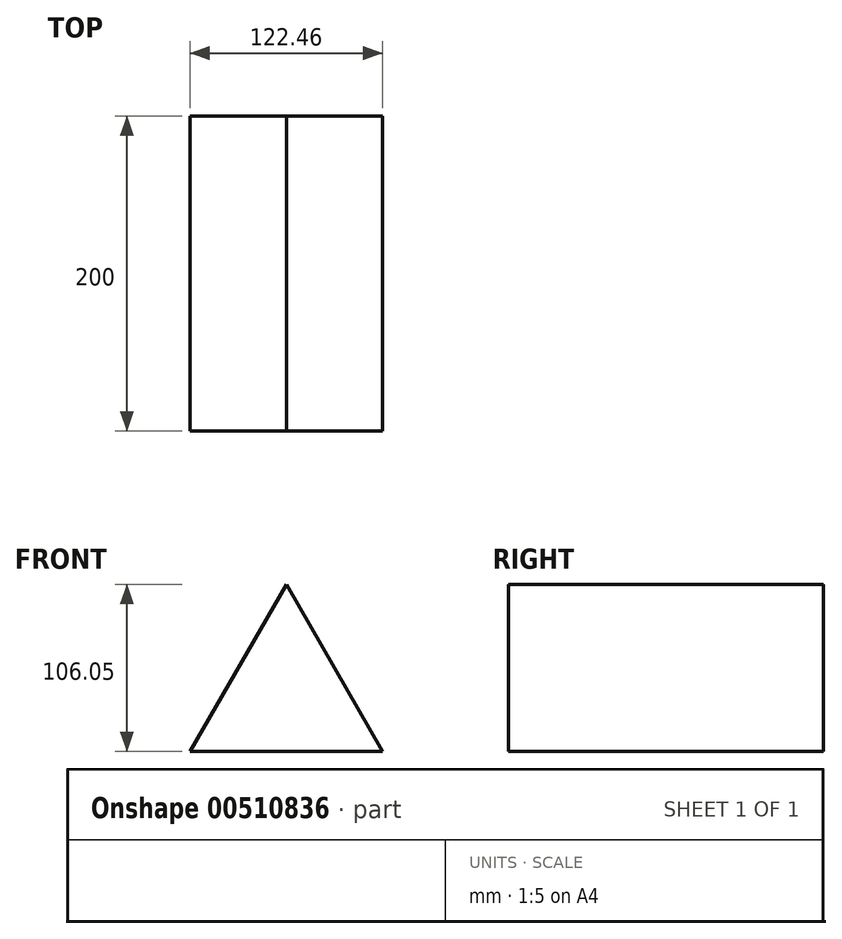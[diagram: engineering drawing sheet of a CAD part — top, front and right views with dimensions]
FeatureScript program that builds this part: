
annotation { "Feature Type Name" : "Feature", "Feature Type Description" : "" }
export const myFeature = defineFeature(function(context is Context, id is Id, definition is map)
    precondition{}
    {
        {
            var Q0;
            Q0=qCreatedBy(makeId("Front.planeOp"),FACE);
            var sketch = newSketch(context, id + "F0", { "sketchPlane" : qUnion([Q0])});
            skCircle(sketch, "E0.cCircle", {"center": v(0, 0) * mm, "radius": 70.7 * mm, "construction": true});
            skLineSegment(sketch, "E0.0", {"start": v(61.23, -35.35) * mm, "end": v(0, 70.7) * mm});
            skLineSegment(sketch, "E0.1", {"start": v(-61.23, -35.35) * mm, "end": v(61.23, -35.35) * mm});
            skLineSegment(sketch, "E0.2", {"start": v(0, 70.7) * mm, "end": v(-61.23, -35.35) * mm});
            skSolve(sketch);
        }
        {
            var Q0;
            Q0=qSketchRegion(id+"F0",true);
            extrude(context, id + "F1", {"entities" : qUnion([Q0]), "depth" : 200 * mm});
        }
    });
